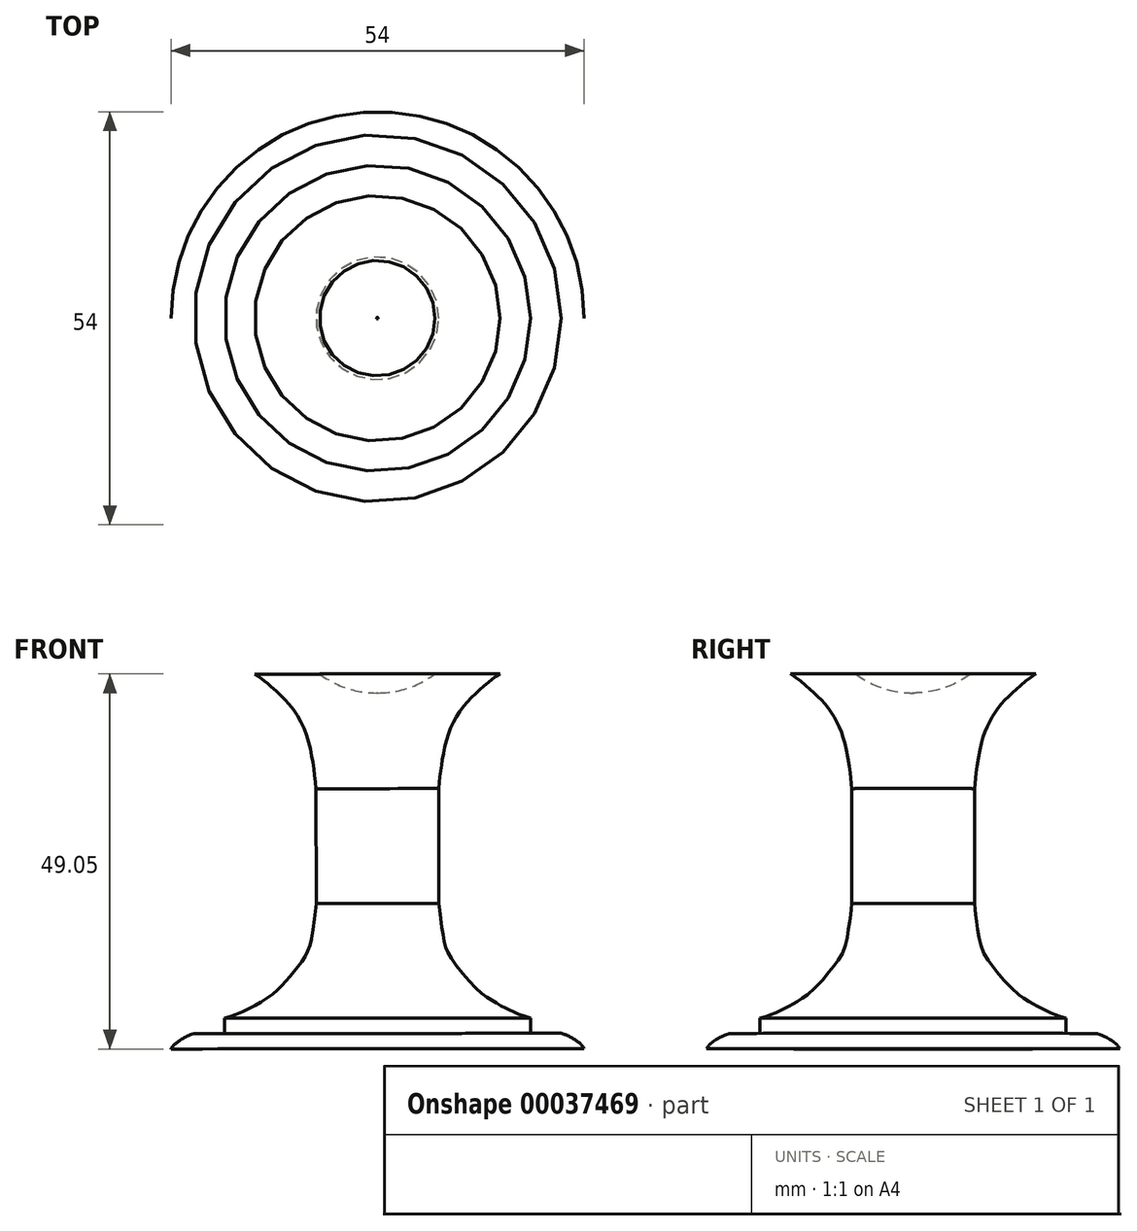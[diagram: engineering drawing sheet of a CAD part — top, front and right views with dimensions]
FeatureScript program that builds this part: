
annotation { "Feature Type Name" : "Feature", "Feature Type Description" : "" }
export const myFeature = defineFeature(function(context is Context, id is Id, definition is map)
    precondition{}
    {
        {
            var Q0;
            Q0=qCreatedBy(makeId("Front.planeOp"),FACE);
            var sketch = newSketch(context, id + "F0", { "sketchPlane" : qUnion([Q0])});
            skArc(sketch, "E0", {"start": v(0.02, -17.96) * mm, "mid": v(0.04, -17.96) * mm, "end": v(0.06, -17.96) * mm});
            skLineSegment(sketch, "E1", {"start": v(7.56, -15.46) * mm, "end": v(16.06, -15.46) * mm});
            skLineSegment(sketch, "E2", {"start": v(8.06, -30.46) * mm, "end": v(8.06, -45.46) * mm});
            skLineSegment(sketch, "E3", {"start": v(20.06, -62.46) * mm, "end": v(24.06, -62.46) * mm});
            skLineSegment(sketch, "E4", {"start": v(0.06, -64.46) * mm, "end": v(27.06, -64.46) * mm});
            skLineSegment(sketch, "E5", {"start": v(20.06, -60.46) * mm, "end": v(20.06, -62.46) * mm});
            skArc(sketch, "E6.trimOffspring", {"start": v(7.56, -15.46) * mm, "mid": v(11.9, -1.48) * mm, "end": v(0, 7.04) * mm});
            skFitSpline(sketch, "E7", {"points": [v(16.06, -15.46) * mm, v(14.88, -16.28) * mm, v(13.38, -17.58) * mm, v(11.89, -19.01) * mm, v(10.4, -21.03) * mm, v(9.32, -23.3) * mm, v(8.63, -26.07) * mm, v(8.3, -28.19) * mm, v(8.06, -30.46) * mm], "startDerivative": vector(-11.46, -7.54) * mm, "endDerivative": vector(-0.93, -17.77) * mm});
            skFitSpline(sketch, "E8", {"points": [v(8.06, -45.46) * mm, v(8.48, -48.71) * mm, v(8.92, -51.05) * mm, v(9.9, -52.95) * mm, v(12.98, -56.6) * mm, v(14.78, -58.01) * mm, v(16.12, -58.82) * mm, v(17.12, -59.32) * mm, v(18.21, -59.82) * mm, v(20.06, -60.46) * mm], "startDerivative": vector(1.32, -17.62) * mm, "endDerivative": vector(17.9, -3.34) * mm});
            skFitSpline(sketch, "E9", {"points": [v(24.06, -62.46) * mm, v(24.67, -62.67) * mm, v(25.38, -63.02) * mm, v(26.12, -63.5) * mm, v(26.61, -63.88) * mm, v(27.06, -64.46) * mm], "startDerivative": vector(3.8, -1.09) * mm, "endDerivative": vector(1.14, -2.86) * mm});
            skLineSegment(sketch, "E10", {"start": v(0, 7.04) * mm, "end": v(0.06, -64.46) * mm});
            skSolve(sketch);
        }
        {
            var Q0;
            Q0=makeQuery(id+"F0.imprint","IMPRINT",FACE,{"disambiguationData":[TD([[makeQuery(id+"F0.imprint","IMPRINT",EDGE,{"derivedFrom":sQuery(id+"F0.wireOp",EDGE,"E1")}),-1.0]])]});
            var Q1;
            Q1=sQuery(id+"F0.wireOp",EDGE,"E10");
            revolve(context, id + "F1", {"entities" : qUnion([Q0]), "axis" : qUnion([Q1]), "revolveType" : RevolveType.FULL});
        }
    });
